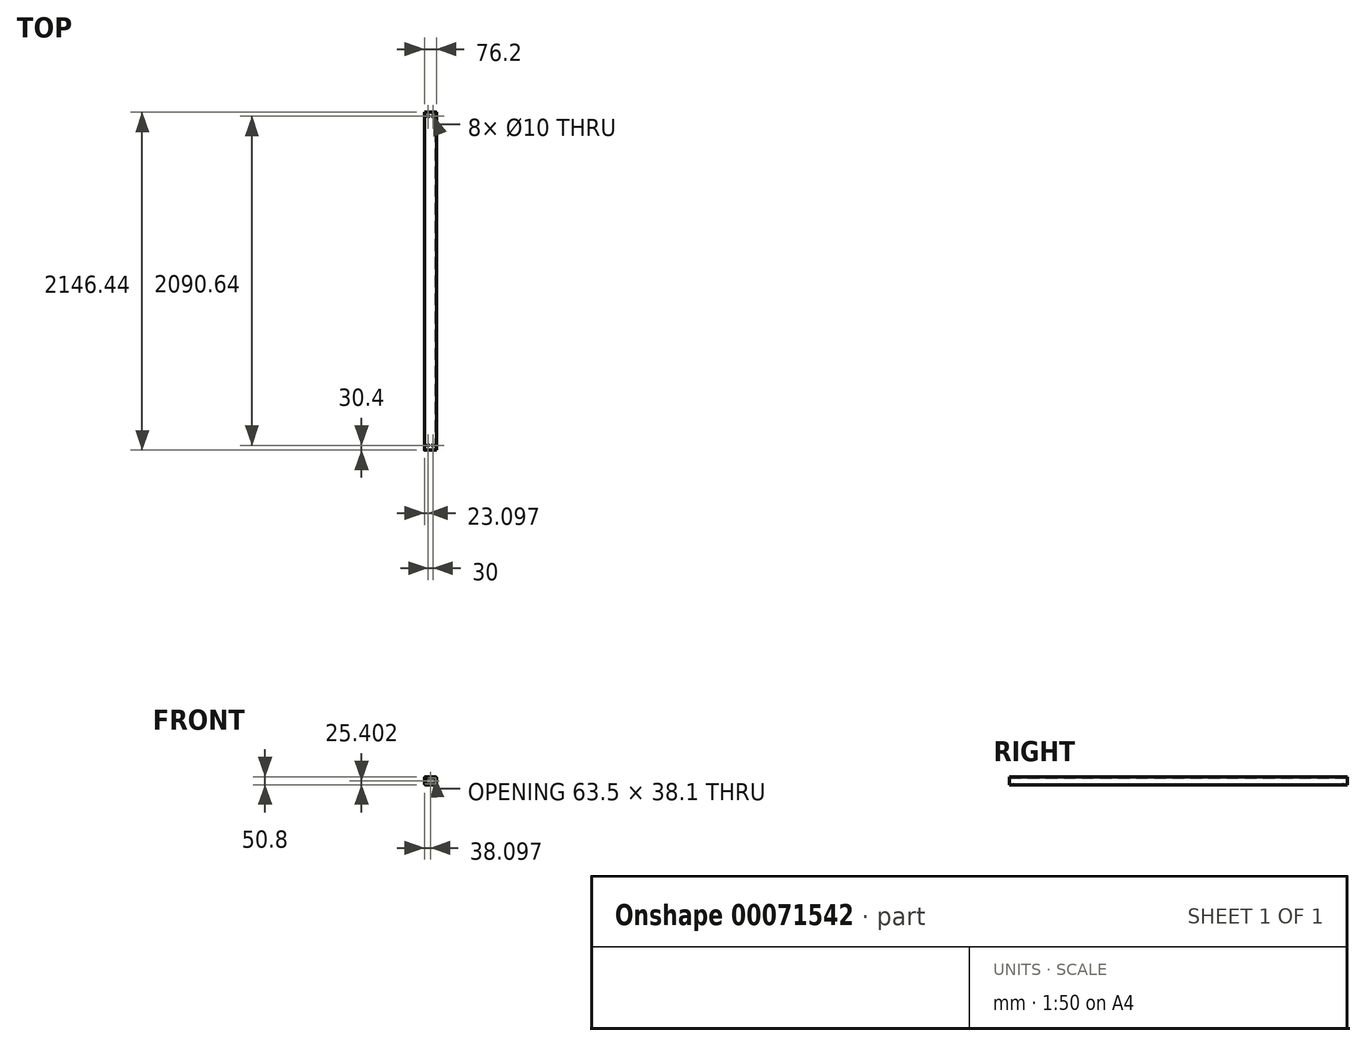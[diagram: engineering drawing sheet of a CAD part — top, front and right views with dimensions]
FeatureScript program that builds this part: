
annotation { "Feature Type Name" : "Feature", "Feature Type Description" : "" }
export const myFeature = defineFeature(function(context is Context, id is Id, definition is map)
    precondition{}
    {
        {
            var Q0;
            Q0=qCreatedBy(makeId("Front.planeOp"),FACE);
            var sketch = newSketch(context, id + "F0", { "sketchPlane" : qUnion([Q0])});
            skLineSegment(sketch, "E0.bottom", {"start": v(-28.92, 22.52) * mm, "end": v(34.58, 22.52) * mm});
            skLineSegment(sketch, "E0.top", {"start": v(-28.92, -28.28) * mm, "end": v(34.58, -28.28) * mm});
            skLineSegment(sketch, "E0.left", {"start": v(-35.27, 16.17) * mm, "end": v(-35.27, -21.93) * mm});
            skLineSegment(sketch, "E0.right", {"start": v(40.93, 16.17) * mm, "end": v(40.93, -21.93) * mm});
            skLineSegment(sketch, "E1.bottom", {"start": v(-22.57, 16.17) * mm, "end": v(28.23, 16.17) * mm});
            skLineSegment(sketch, "E1.top", {"start": v(-22.57, -21.93) * mm, "end": v(28.23, -21.93) * mm});
            skLineSegment(sketch, "E1.left", {"start": v(-28.92, 9.82) * mm, "end": v(-28.92, -15.58) * mm});
            skLineSegment(sketch, "E1.right", {"start": v(34.58, 9.82) * mm, "end": v(34.58, -15.58) * mm});
            skPoint(sketch, "E2.visualSharp", {"position": v(-28.92, 16.17) * mm});
            skArc(sketch, "E2.filletArc", {"start": v(-22.57, 16.17) * mm, "mid": v(-27.06, 14.31) * mm, "end": v(-28.92, 9.82) * mm});
            skPoint(sketch, "E3.visualSharp", {"position": v(-28.92, -21.93) * mm});
            skArc(sketch, "E3.filletArc", {"start": v(-28.92, -15.58) * mm, "mid": v(-27.06, -20.07) * mm, "end": v(-22.57, -21.93) * mm});
            skPoint(sketch, "E4.visualSharp", {"position": v(34.58, -21.93) * mm});
            skArc(sketch, "E4.filletArc", {"start": v(28.23, -21.93) * mm, "mid": v(32.72, -20.07) * mm, "end": v(34.58, -15.58) * mm});
            skPoint(sketch, "E5.visualSharp", {"position": v(34.58, 16.17) * mm});
            skArc(sketch, "E5.filletArc", {"start": v(34.58, 9.82) * mm, "mid": v(32.72, 14.31) * mm, "end": v(28.23, 16.17) * mm});
            skPoint(sketch, "E6.visualSharp", {"position": v(40.93, 22.52) * mm});
            skArc(sketch, "E6.filletArc", {"start": v(40.93, 16.17) * mm, "mid": v(39.07, 20.66) * mm, "end": v(34.58, 22.52) * mm});
            skPoint(sketch, "E7.visualSharp", {"position": v(40.93, -28.28) * mm});
            skArc(sketch, "E7.filletArc", {"start": v(34.58, -28.28) * mm, "mid": v(39.07, -26.42) * mm, "end": v(40.93, -21.93) * mm});
            skPoint(sketch, "E8.visualSharp", {"position": v(-35.27, -28.28) * mm});
            skArc(sketch, "E8.filletArc", {"start": v(-35.27, -21.93) * mm, "mid": v(-33.41, -26.42) * mm, "end": v(-28.92, -28.28) * mm});
            skPoint(sketch, "E9.visualSharp", {"position": v(-35.27, 22.52) * mm});
            skArc(sketch, "E9.filletArc", {"start": v(-28.92, 22.52) * mm, "mid": v(-33.41, 20.66) * mm, "end": v(-35.27, 16.17) * mm});
            skSolve(sketch);
        }
        {
            var Q0;
            Q0 = qSketchRegion(id + "F0", true);
            extrude(context, id + "F1", {"entities" : qUnion([Q0]), "depth" : 2146.44 * mm});
        }
        {
            var Q0;
            Q0=makeQuery(id+"F1.opExtrude","SWEPT_FACE",FACE,{"disambiguationData":[OSD([sQuery(id+"F0.wireOp",EDGE,"E0.top")])]});
            var sketch = newSketch(context, id + "F2", { "sketchPlane" : qUnion([Q0])});
            skCircle(sketch, "E10", {"center": v(17.83, 2116.04) * mm, "radius": 5 * mm});
            skCircle(sketch, "E11", {"center": v(-12.17, 2116.04) * mm, "radius": 5 * mm});
            skCircle(sketch, "E12", {"center": v(17.83, 25.4) * mm, "radius": 5 * mm});
            skCircle(sketch, "E13", {"center": v(-12.17, 25.4) * mm, "radius": 5 * mm});
            skSolve(sketch);
        }
        {
            var Q0;
            Q0 = qSketchRegion(id + "F2", true);
            extrude(context, id + "F3", {"entities" : qUnion([Q0]), "operationType" : NewBodyOperationType.REMOVE, "endBound" : BoundingType.THROUGH_ALL, "oppositeDirection" : true, "depth" : 25 * mm});
        }
    });
